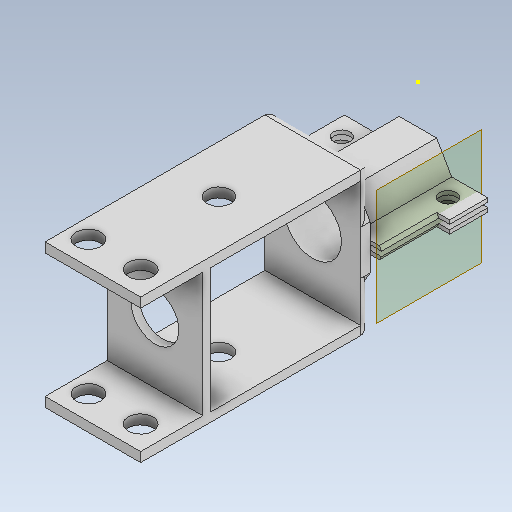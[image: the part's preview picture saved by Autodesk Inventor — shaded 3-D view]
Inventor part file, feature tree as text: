
AUTODESK INVENTOR PART (.ipt)
format: ipt  version: 2021 (Build 250183000, 183)  size: 289,792 bytes
history: native  units: mm
features: sketch x17, other x3, plane x1
ambient origin geometry x8: Origin, YZ Plane, XZ Plane, XY Plane, X Axis, Y Axis, Z Axis, Center Point
bodies: Solid1 (feature_tree)
feature tree (21):
  other  "suction_cup_holder.ipt"
  other  "Solid1::suction_cup_holder.ipt"
  other  "TaggingFeature1"
  sketch  "Sketch1"  dims[d0=10.0mm]
  sketch  "Sketch4"
  sketch  "Sketch5"
  sketch  "Sketch6"
  sketch  "Sketch7"
  sketch  "Sketch8"
  sketch  "Sketch9"
  sketch  "Sketch10"
  sketch  "Sketch11"
  sketch  "Sketch12"
  sketch  "Sketch14"
  sketch  "Sketch16"
  sketch  "Sketch17"
  sketch  "Sketch18"
  sketch  "Sketch19"
  sketch  "Sketch20"
  sketch  "Sketch21"
  plane  "Work Plane1"
